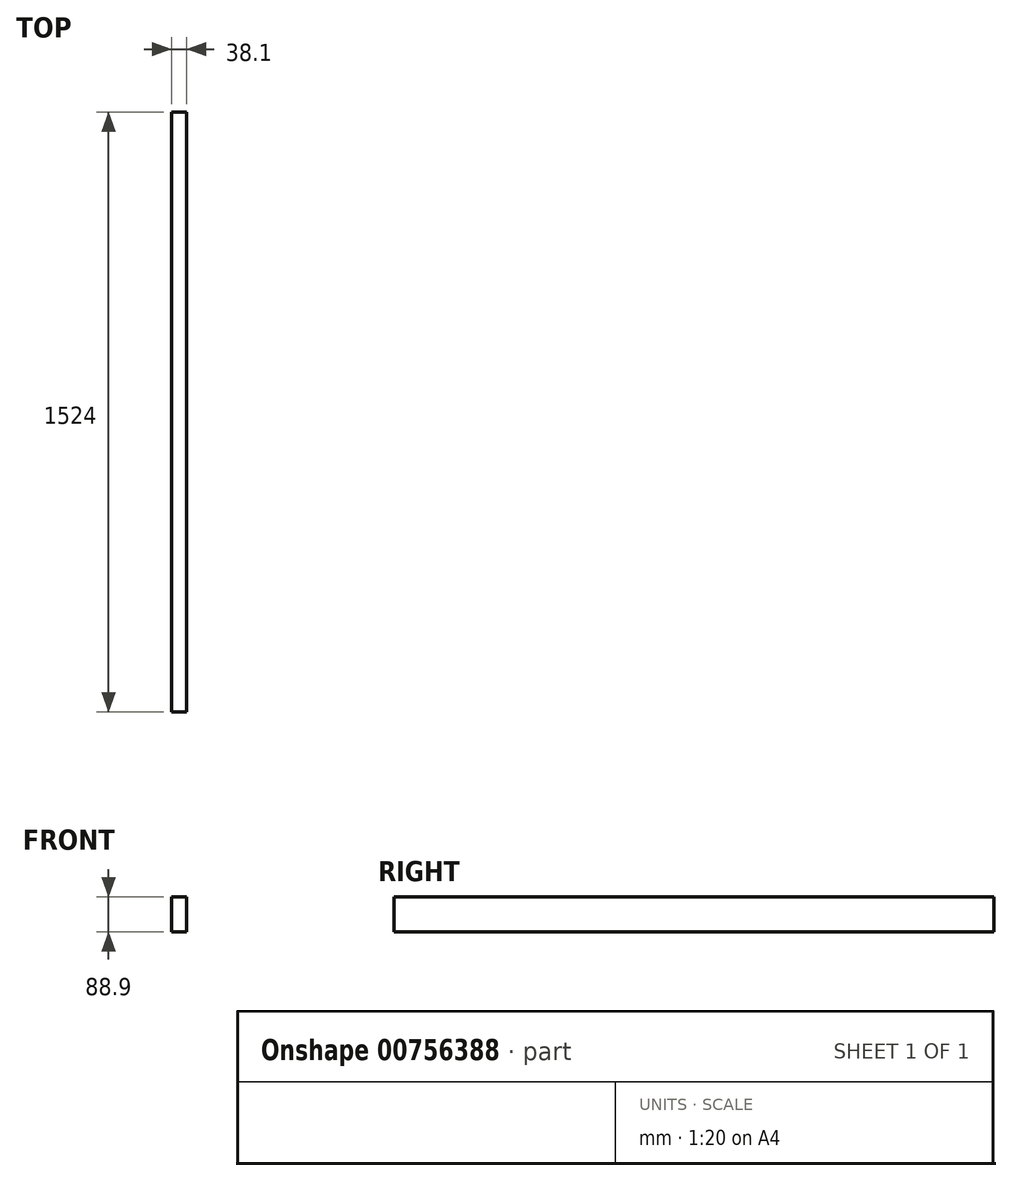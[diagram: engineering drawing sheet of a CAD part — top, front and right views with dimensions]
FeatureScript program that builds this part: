
annotation { "Feature Type Name" : "Feature", "Feature Type Description" : "" }
export const myFeature = defineFeature(function(context is Context, id is Id, definition is map)
    precondition{}
    {
        {
            var Q0;
            Q0=qCreatedBy(makeId("Front.planeOp"),FACE);
            var sketch = newSketch(context, id + "F0", { "sketchPlane" : qUnion([Q0])});
            skLineSegment(sketch, "E0.bottom", {"start": v(0, 0) * mm, "end": v(38.1, 0) * mm});
            skLineSegment(sketch, "E0.top", {"start": v(0, 88.9) * mm, "end": v(38.1, 88.9) * mm});
            skLineSegment(sketch, "E0.left", {"start": v(0, 0) * mm, "end": v(0, 88.9) * mm});
            skLineSegment(sketch, "E0.right", {"start": v(38.1, 0) * mm, "end": v(38.1, 88.9) * mm});
            skSolve(sketch);
        }
        {
            var Q0;
            Q0=makeQuery(id+"F0.imprint","IMPRINT",FACE,{"disambiguationData":[TD([[makeQuery(id+"F0.imprint","IMPRINT",EDGE,{"derivedFrom":sQuery(id+"F0.wireOp",EDGE,"E0.bottom")}),1.0]])]});
            extrude(context, id + "F1", {"entities" : qUnion([Q0]), "depth" : 1524 * mm, "offsetDistance" : 25.4 * mm});
        }
    });
